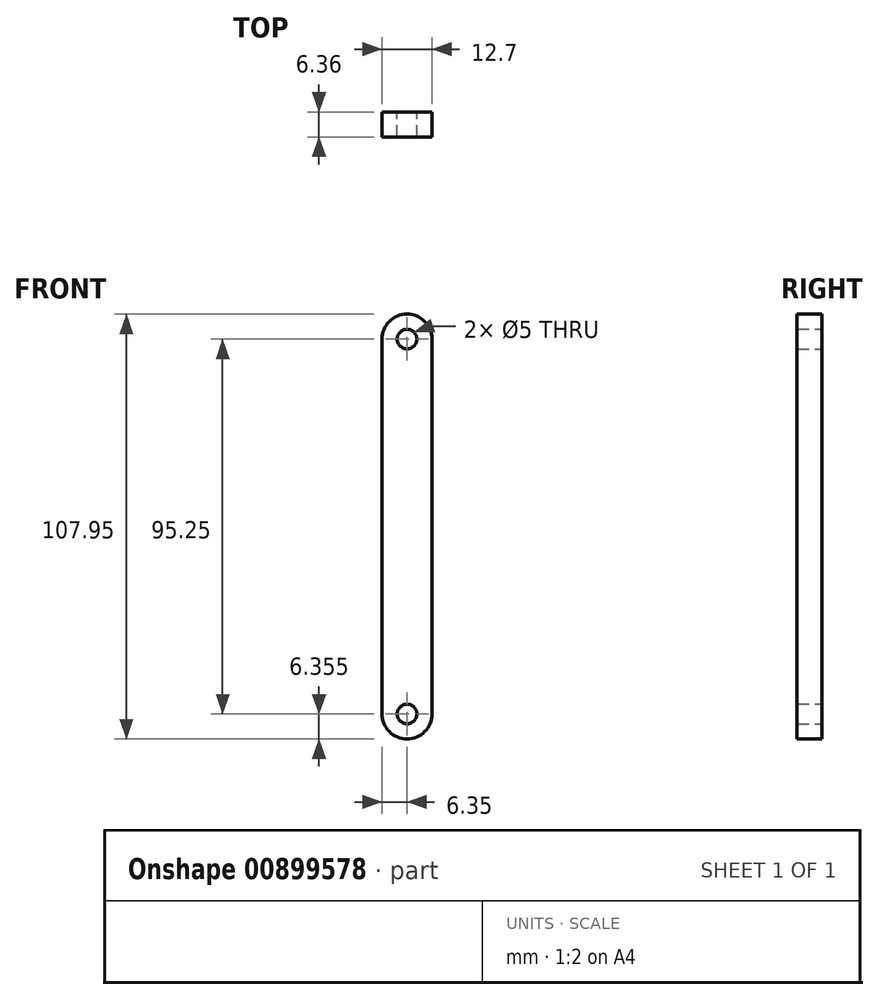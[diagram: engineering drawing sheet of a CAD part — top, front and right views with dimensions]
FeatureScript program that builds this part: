
annotation { "Feature Type Name" : "Feature", "Feature Type Description" : "" }
export const myFeature = defineFeature(function(context is Context, id is Id, definition is map)
    precondition{}
    {
        {
            var Q0;
            Q0=qCreatedBy(makeId("Front.planeOp"),FACE);
            var sketch = newSketch(context, id + "F0", { "sketchPlane" : qUnion([Q0])});
            skLineSegment(sketch, "E0", {"start": v(-12.7, 47.62) * mm, "end": v(-12.7, -47.62) * mm});
            skLineSegment(sketch, "E1", {"start": v(0, 47.62) * mm, "end": v(0, -47.62) * mm});
            skArc(sketch, "E2", {"start": v(0, 47.62) * mm, "mid": v(-6.35, 53.97) * mm, "end": v(-12.7, 47.62) * mm});
            skArc(sketch, "E3", {"start": v(-12.7, -47.62) * mm, "mid": v(-6.35, -53.98) * mm, "end": v(0, -47.62) * mm});
            skCircle(sketch, "E4", {"center": v(-6.35, 47.62) * mm, "radius": 2.5 * mm});
            skCircle(sketch, "E5", {"center": v(-6.35, -47.63) * mm, "radius": 2.5 * mm});
            skLineSegment(sketch, "E6", {"start": v(-12.7, 0) * mm, "end": v(0, 0) * mm});
            skSolve(sketch);
        }
        {
            var Q0;
            {var subQ0=sQuery(id+"F0.wireOp",EDGE,"E2");Q0=makeQuery(id+"F0.imprint","IMPRINT",FACE,{"disambiguationData":[TD([[makeQuery(id+"F0.imprint","IMPRINT",EDGE,{"derivedFrom":subQ0}),1.0]])]});}
            var Q1;
            {var subQ0=sQuery(id+"F0.wireOp",EDGE,"E3");Q1=makeQuery(id+"F0.imprint","IMPRINT",FACE,{"disambiguationData":[TD([[makeQuery(id+"F0.imprint","IMPRINT",EDGE,{"derivedFrom":subQ0}),1.0]])]});}
            extrude(context, id + "F1", {"entities" : qUnion([Q0, Q1]), "endBound" : BoundingType.SYMMETRIC, "depth" : 6.35 * mm, "offsetDistance" : 25.4 * mm});
        }
    });
